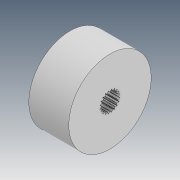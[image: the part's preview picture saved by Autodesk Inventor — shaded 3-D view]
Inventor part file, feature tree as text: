
AUTODESK INVENTOR PART (.ipt)
format: ipt  version: 2021 (Build 250183000, 183)  size: 265,728 bytes
history: native  units: in
note: dims shown in document units (in); Inventor stores cm internally (conversion verified against a paired STEP export)
features: sketch x4, extrude x3, other x2
ambient origin geometry x8: Origin, YZ Plane, XZ Plane, XY Plane, X Axis, Y Axis, Z Axis, Center Point
bodies: Body1 (feature_tree)
feature tree (9):
  other  "Sólido1"
  other  "Revolução1"
  extrude  "Extrusão1"  Depth=0.3858in
  extrude  "Extrusão2"  Depth=0.1378in
  extrude  "Extrusão3"  Depth=0.1909in
  sketch  "Esboço2"  dims[d0=0.374in d1=0.3858in]
  sketch  "Esboço3"  dims[d2=90.0deg d3=0.1378in]
  sketch  "Esboço4"  dims[d4=0.1909in d5=0.0in d6=0.3543in]
  sketch  "Esboço8"  dims[d7=0.0787in d8=0.0in d35=0.1575in d36=0.189in d37=0.002in d38=0.002in d39=0.002in d40=0.1378in d41=0.0in d42=7.874in d44=360.0deg]
